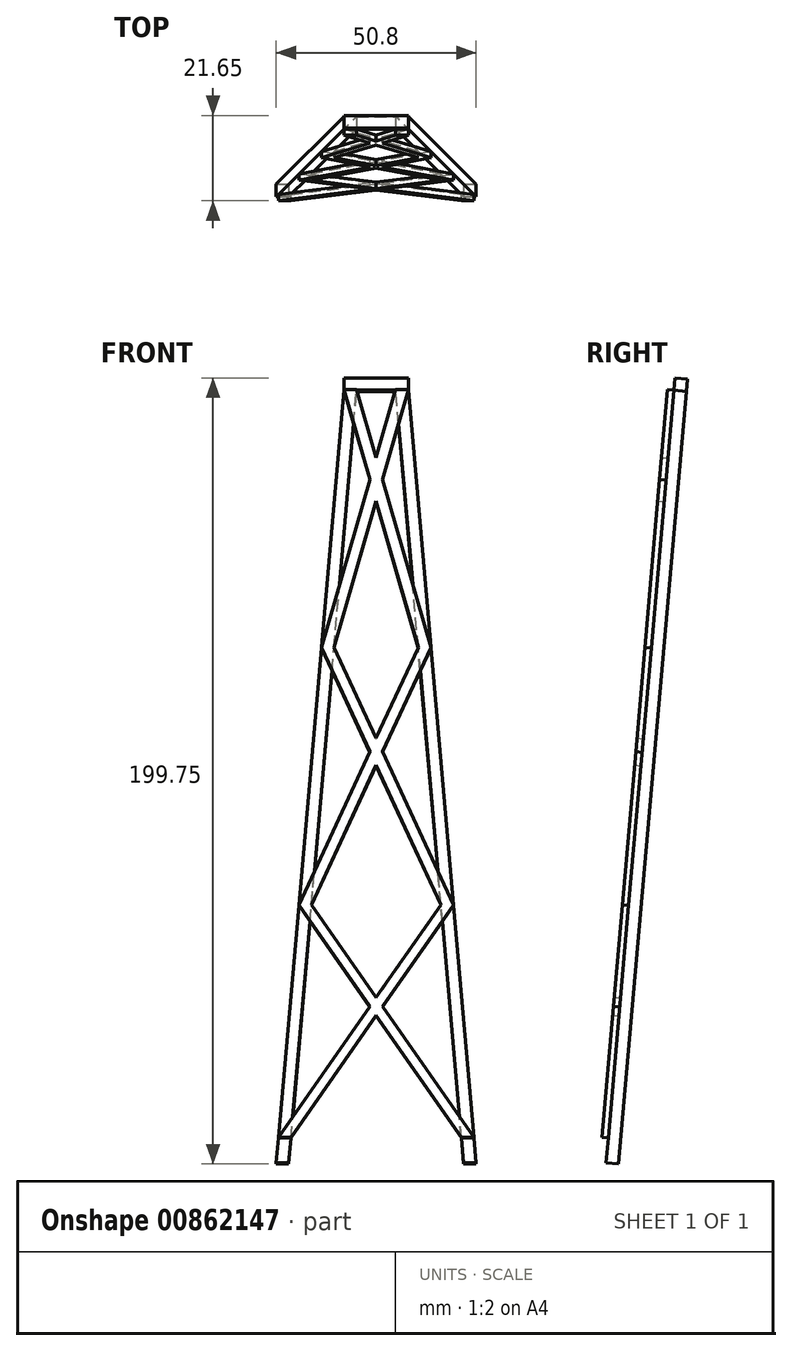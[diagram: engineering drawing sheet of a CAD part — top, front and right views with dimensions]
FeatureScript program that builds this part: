
annotation { "Feature Type Name" : "Feature", "Feature Type Description" : "" }
export const myFeature = defineFeature(function(context is Context, id is Id, definition is map)
    precondition{}
    {
        {
            var Q0;
            Q0=qCreatedBy(makeId("Top.planeOp"),FACE);
            var sketch = newSketch(context, id + "F0", { "sketchPlane" : qUnion([Q0])});
            skLineSegment(sketch, "E0", {"start": v(0, 0) * mm, "end": v(0, 116.82) * mm, "construction": true});
            skLineSegment(sketch, "E1", {"start": v(0, 0) * mm, "end": v(-140.82, 0) * mm, "construction": true});
            skSolve(sketch);
        }
        {
            var Q0;
            Q0=qCreatedBy(makeId("Right.planeOp"),FACE);
            var sketch = newSketch(context, id + "F1", { "sketchPlane" : qUnion([Q0])});
            skLineSegment(sketch, "E2", {"start": v(0, 0) * mm, "end": v(0, 196.85) * mm, "construction": true});
            skSolve(sketch);
        }
        {
            var Q0;
            Q0=qCreatedBy(makeId("Right.planeOp"),FACE);
            var sketch = newSketch(context, id + "F2", { "sketchPlane" : qUnion([Q0])});
            skPoint(sketch, "E3", {"position": v(-25.4, 0) * mm});
            skPoint(sketch, "E4.MirrorP", {"position": v(25.4, 0) * mm});
            skPoint(sketch, "E5", {"position": v(0, 290.32) * mm});
            skLineSegment(sketch, "E6", {"start": v(0, 290.32) * mm, "end": v(-25.4, 0) * mm, "construction": true});
            skLineSegment(sketch, "E7", {"start": v(0, 197.07) * mm, "end": v(-8.16, 197.07) * mm, "construction": true});
            skSolve(sketch);
        }
        {
            var Q0;
            Q0=sQuery(id+"F2.wireOp",EDGE,"E6");
            cPlane(context, id + "F3", {"entities" : qUnion([Q0]), "cplaneType" : CPlaneType.LINE_ANGLE, "offset" : 25.4 * mm, "angle" : 270 * degree, "width" : 152.4 * mm, "height" : 152.4 * mm});
        }
        {
            var Q0;
            Q0=qCreatedBy(id+"F3.planeOp",FACE);
            var sketch = newSketch(context, id + "F4", { "sketchPlane" : qUnion([Q0])});
            skLineSegment(sketch, "E8", {"start": v(-8.16, 197.06) * mm, "end": v(-25.4, 0) * mm});
            skLineSegment(sketch, "E9.0", {"start": v(-22.21, 0) * mm, "end": v(-4.97, 197.06) * mm});
            skLineSegment(sketch, "E10", {"start": v(-25.4, 0) * mm, "end": v(-22.24, 0) * mm});
            skPoint(sketch, "E11.orphan", {"position": v(0, 290.32) * mm});
            skLineSegment(sketch, "E12.MirrorCS", {"start": v(8.16, 197.06) * mm, "end": v(25.4, 0) * mm});
            skLineSegment(sketch, "E13.MirrorCS", {"start": v(22.21, 0) * mm, "end": v(4.97, 197.06) * mm});
            skLineSegment(sketch, "E14", {"start": v(-8.16, 197.06) * mm, "end": v(-4.97, 197.06) * mm});
            skLineSegment(sketch, "E15", {"start": v(-25.4, 0) * mm, "end": v(-22.21, 0) * mm});
            skLineSegment(sketch, "E16", {"start": v(4.97, 197.06) * mm, "end": v(8.16, 197.06) * mm});
            skLineSegment(sketch, "E17", {"start": v(22.21, 0) * mm, "end": v(25.4, 0) * mm});
            skLineSegment(sketch, "E18", {"start": v(-8.16, 197.06) * mm, "end": v(8.16, 197.06) * mm});
            skLineSegment(sketch, "E19", {"start": v(8.16, 200.23) * mm, "end": v(8.16, 197.06) * mm});
            skLineSegment(sketch, "E20", {"start": v(8.16, 200.23) * mm, "end": v(-8.16, 200.23) * mm});
            skLineSegment(sketch, "E21", {"start": v(-8.16, 200.23) * mm, "end": v(-8.16, 197.06) * mm});
            skLineSegment(sketch, "E22", {"start": v(52.04, 197.06) * mm, "end": v(52.04, 0) * mm, "construction": true});
            skLineSegment(sketch, "E23", {"start": v(31.34, 0) * mm, "end": v(31.34, 6.35) * mm, "construction": true});
            skLineSegment(sketch, "E24", {"start": v(31.34, 6.35) * mm, "end": v(-63.34, 6.35) * mm, "construction": true});
            skLineSegment(sketch, "E25", {"start": v(24.84, 6.35) * mm, "end": v(21.66, 6.35) * mm});
            skLineSegment(sketch, "E26", {"start": v(40.88, 197.06) * mm, "end": v(40.88, 131.37) * mm, "construction": true});
            skLineSegment(sketch, "E27", {"start": v(40.88, 131.37) * mm, "end": v(40.88, 65.69) * mm, "construction": true});
            skLineSegment(sketch, "E28", {"start": v(40.88, 65.69) * mm, "end": v(40.88, 0) * mm, "construction": true});
            skLineSegment(sketch, "E29", {"start": v(40.88, 65.69) * mm, "end": v(-70.33, 65.69) * mm, "construction": true});
            skLineSegment(sketch, "E30", {"start": v(40.88, 131.37) * mm, "end": v(-29.1, 131.37) * mm, "construction": true});
            skLineSegment(sketch, "E31", {"start": v(-4.97, 197.06) * mm, "end": v(13.9, 131.37) * mm});
            skLineSegment(sketch, "E32", {"start": v(13.9, 131.37) * mm, "end": v(10.72, 131.37) * mm});
            skLineSegment(sketch, "E33", {"start": v(10.72, 131.37) * mm, "end": v(-8.16, 197.06) * mm});
            skLineSegment(sketch, "E34", {"start": v(-10.72, 131.37) * mm, "end": v(19.65, 65.69) * mm});
            skLineSegment(sketch, "E35", {"start": v(19.65, 65.69) * mm, "end": v(16.47, 65.69) * mm});
            skLineSegment(sketch, "E36", {"start": v(16.47, 65.69) * mm, "end": v(-13.9, 131.37) * mm});
            skLineSegment(sketch, "E37", {"start": v(-13.9, 131.37) * mm, "end": v(-10.72, 131.37) * mm});
            skLineSegment(sketch, "E38", {"start": v(-16.47, 65.69) * mm, "end": v(24.84, 6.35) * mm});
            skLineSegment(sketch, "E39", {"start": v(21.66, 6.35) * mm, "end": v(-19.65, 65.69) * mm});
            skLineSegment(sketch, "E40", {"start": v(-19.65, 65.69) * mm, "end": v(-16.47, 65.69) * mm});
            skLineSegment(sketch, "E41", {"start": v(4.97, 197.06) * mm, "end": v(-13.9, 131.37) * mm});
            skLineSegment(sketch, "E42", {"start": v(-10.72, 131.37) * mm, "end": v(8.16, 197.06) * mm});
            skLineSegment(sketch, "E43", {"start": v(-19.65, 65.69) * mm, "end": v(10.72, 131.37) * mm});
            skLineSegment(sketch, "E44", {"start": v(13.9, 131.37) * mm, "end": v(-16.47, 65.69) * mm});
            skLineSegment(sketch, "E45", {"start": v(16.47, 65.69) * mm, "end": v(-24.84, 6.35) * mm});
            skLineSegment(sketch, "E46", {"start": v(-24.84, 6.35) * mm, "end": v(-21.66, 6.35) * mm});
            skLineSegment(sketch, "E47", {"start": v(-21.66, 6.35) * mm, "end": v(19.65, 65.69) * mm});
            skSolve(sketch);
        }
        {
            var Q0;
            {var subQ0=sQuery(id+"F4.wireOp",EDGE,"E19");Q0=makeQuery(id+"F4.imprint","IMPRINT",FACE,{"disambiguationData":[TD([[makeQuery(id+"F4.imprint","IMPRINT",EDGE,{"derivedFrom":subQ0}),-1.0]])]});}
            extrude(context, id + "F5", {"entities" : qUnion([Q0]), "oppositeDirection" : true, "depth" : 3.17 * mm, "offsetDistance" : 25.4 * mm});
        }
        {
            var Q0;
            {var subQ1=sQuery(id+"F4.wireOp",EDGE,"E9.0");var subQ3=sQuery(id+"F4.wireOp",EDGE,"E33");var subQ4=makeQuery(id+"F4.imprint","INTERSECT",VERTEX,{"derivedFrom":[subQ1,subQ3]});Q0=makeQuery(id+"F4.imprint","IMPRINT",FACE,{"disambiguationData":[TD([[makeQuery(id+"F4.imprint","IMPRINT",EDGE,{"disambiguationData":[TD([[subQ4,-1.0]])],"derivedFrom":subQ1}),1.0]])]});}
            var Q1;
            {var subQ3=sQuery(id+"F4.wireOp",EDGE,"E41");var subQ5=sQuery(id+"F4.wireOp",EDGE,"E9.0");var subQ6=makeQuery(id+"F4.imprint","INTERSECT",VERTEX,{"derivedFrom":[subQ5,subQ3]});Q1=makeQuery(id+"F4.imprint","IMPRINT",FACE,{"disambiguationData":[TD([[makeQuery(id+"F4.imprint","IMPRINT",EDGE,{"disambiguationData":[TD([[subQ6,-1.0]])],"derivedFrom":subQ5}),1.0]])]});}
            var Q2;
            {var subQ1=sQuery(id+"F4.wireOp",EDGE,"E13.MirrorCS");var subQ3=sQuery(id+"F4.wireOp",EDGE,"E42");var subQ4=makeQuery(id+"F4.imprint","INTERSECT",VERTEX,{"derivedFrom":[subQ1,subQ3]});Q2=makeQuery(id+"F4.imprint","IMPRINT",FACE,{"disambiguationData":[TD([[makeQuery(id+"F4.imprint","IMPRINT",EDGE,{"disambiguationData":[TD([[subQ4,-1.0]])],"derivedFrom":subQ1}),-1.0]])]});}
            var Q3;
            {var subQ3=sQuery(id+"F4.wireOp",EDGE,"E31");var subQ5=sQuery(id+"F4.wireOp",EDGE,"E13.MirrorCS");var subQ6=makeQuery(id+"F4.imprint","INTERSECT",VERTEX,{"derivedFrom":[subQ5,subQ3]});Q3=makeQuery(id+"F4.imprint","IMPRINT",FACE,{"disambiguationData":[TD([[makeQuery(id+"F4.imprint","IMPRINT",EDGE,{"disambiguationData":[TD([[subQ6,-1.0]])],"derivedFrom":subQ5}),-1.0]])]});}
            var Q4;
            {var subQ0=sQuery(id+"F4.wireOp",EDGE,"E32");Q4=makeQuery(id+"F4.imprint","IMPRINT",FACE,{"disambiguationData":[TD([[makeQuery(id+"F4.imprint","IMPRINT",EDGE,{"derivedFrom":subQ0}),-1.0]])]});}
            var Q5;
            {var subQ0=sQuery(id+"F4.wireOp",EDGE,"E32");Q5=makeQuery(id+"F4.imprint","IMPRINT",FACE,{"disambiguationData":[TD([[makeQuery(id+"F4.imprint","IMPRINT",EDGE,{"derivedFrom":subQ0}),1.0]])]});}
            var Q6;
            {var subQ0=sQuery(id+"F4.wireOp",EDGE,"E37");Q6=makeQuery(id+"F4.imprint","IMPRINT",FACE,{"disambiguationData":[TD([[makeQuery(id+"F4.imprint","IMPRINT",EDGE,{"derivedFrom":subQ0}),1.0]])]});}
            var Q7;
            {var subQ0=sQuery(id+"F4.wireOp",EDGE,"E37");Q7=makeQuery(id+"F4.imprint","IMPRINT",FACE,{"disambiguationData":[TD([[makeQuery(id+"F4.imprint","IMPRINT",EDGE,{"derivedFrom":subQ0}),-1.0]])]});}
            var Q8;
            {var subQ3=sQuery(id+"F4.wireOp",EDGE,"E43");var subQ5=sQuery(id+"F4.wireOp",EDGE,"E9.0");var subQ6=makeQuery(id+"F4.imprint","INTERSECT",VERTEX,{"derivedFrom":[subQ5,subQ3]});Q8=makeQuery(id+"F4.imprint","IMPRINT",FACE,{"disambiguationData":[TD([[makeQuery(id+"F4.imprint","IMPRINT",EDGE,{"disambiguationData":[TD([[subQ6,-1.0]])],"derivedFrom":subQ5}),1.0]])]});}
            var Q9;
            {var subQ3=sQuery(id+"F4.wireOp",EDGE,"E34");var subQ5=sQuery(id+"F4.wireOp",EDGE,"E13.MirrorCS");var subQ6=makeQuery(id+"F4.imprint","INTERSECT",VERTEX,{"derivedFrom":[subQ5,subQ3]});Q9=makeQuery(id+"F4.imprint","IMPRINT",FACE,{"disambiguationData":[TD([[makeQuery(id+"F4.imprint","IMPRINT",EDGE,{"disambiguationData":[TD([[subQ6,-1.0]])],"derivedFrom":subQ5}),-1.0]])]});}
            var Q10;
            {var subQ0=sQuery(id+"F4.wireOp",EDGE,"E35");Q10=makeQuery(id+"F4.imprint","IMPRINT",FACE,{"disambiguationData":[TD([[makeQuery(id+"F4.imprint","IMPRINT",EDGE,{"derivedFrom":subQ0}),-1.0]])]});}
            var Q11;
            {var subQ0=sQuery(id+"F4.wireOp",EDGE,"E40");Q11=makeQuery(id+"F4.imprint","IMPRINT",FACE,{"disambiguationData":[TD([[makeQuery(id+"F4.imprint","IMPRINT",EDGE,{"derivedFrom":subQ0}),1.0]])]});}
            var Q12;
            {var subQ0=sQuery(id+"F4.wireOp",EDGE,"E40");Q12=makeQuery(id+"F4.imprint","IMPRINT",FACE,{"disambiguationData":[TD([[makeQuery(id+"F4.imprint","IMPRINT",EDGE,{"derivedFrom":subQ0}),-1.0]])]});}
            var Q13;
            {var subQ0=sQuery(id+"F4.wireOp",EDGE,"E35");Q13=makeQuery(id+"F4.imprint","IMPRINT",FACE,{"disambiguationData":[TD([[makeQuery(id+"F4.imprint","IMPRINT",EDGE,{"derivedFrom":subQ0}),1.0]])]});}
            var Q14;
            {var subQ0=sQuery(id+"F4.wireOp",EDGE,"E38");var subQ5=sQuery(id+"F4.wireOp",EDGE,"E13.MirrorCS");var subQ6=makeQuery(id+"F4.imprint","INTERSECT",VERTEX,{"derivedFrom":[subQ5,subQ0]});Q14=makeQuery(id+"F4.imprint","IMPRINT",FACE,{"disambiguationData":[TD([[makeQuery(id+"F4.imprint","IMPRINT",EDGE,{"disambiguationData":[TD([[subQ6,-1.0]])],"derivedFrom":subQ5}),-1.0]])]});}
            var Q15;
            {var subQ3=sQuery(id+"F4.wireOp",EDGE,"E45");var subQ5=sQuery(id+"F4.wireOp",EDGE,"E9.0");var subQ7=makeQuery(id+"F4.imprint","INTERSECT",VERTEX,{"derivedFrom":[subQ5,subQ3]});Q15=makeQuery(id+"F4.imprint","IMPRINT",FACE,{"disambiguationData":[TD([[makeQuery(id+"F4.imprint","IMPRINT",EDGE,{"disambiguationData":[TD([[subQ7,-1.0]])],"derivedFrom":subQ5}),1.0]])]});}
            var Q16;
            {var subQ0=sQuery(id+"F4.wireOp",EDGE,"E46");Q16=makeQuery(id+"F4.imprint","IMPRINT",FACE,{"disambiguationData":[TD([[makeQuery(id+"F4.imprint","IMPRINT",EDGE,{"derivedFrom":subQ0}),1.0]])]});}
            var Q17;
            {var subQ0=sQuery(id+"F4.wireOp",EDGE,"E25");Q17=makeQuery(id+"F4.imprint","IMPRINT",FACE,{"disambiguationData":[TD([[makeQuery(id+"F4.imprint","IMPRINT",EDGE,{"derivedFrom":subQ0}),-1.0]])]});}
            var Q18;
            {var subQ0=sQuery(id+"F4.wireOp",EDGE,"E17");Q18=makeQuery(id+"F4.imprint","IMPRINT",FACE,{"disambiguationData":[TD([[makeQuery(id+"F4.imprint","IMPRINT",EDGE,{"derivedFrom":subQ0}),1.0]])]});}
            var Q19;
            {var subQ3=sQuery(id+"F4.wireOp",EDGE,"E46");Q19=makeQuery(id+"F4.imprint","IMPRINT",FACE,{"disambiguationData":[TD([[makeQuery(id+"F4.imprint","IMPRINT",EDGE,{"derivedFrom":subQ3}),-1.0]])]});}
            extrude(context, id + "F6", {"entities" : qUnion([Q0, Q1, Q2, Q3, Q4, Q5, Q6, Q7, Q8, Q9, Q10, Q11, Q12, Q13, Q14, Q15, Q16, Q17, Q18, Q19]), "oppositeDirection" : true, "depth" : 3.17 * mm, "offsetDistance" : 25.4 * mm});
        }
        {
            var Q0;
            {var subQ1=sQuery(id+"F4.wireOp",EDGE,"E9.0");var subQ3=sQuery(id+"F4.wireOp",EDGE,"E33");var subQ4=makeQuery(id+"F4.imprint","INTERSECT",VERTEX,{"derivedFrom":[subQ1,subQ3]});Q0=makeQuery(id+"F4.imprint","IMPRINT",FACE,{"disambiguationData":[TD([[makeQuery(id+"F4.imprint","IMPRINT",EDGE,{"disambiguationData":[TD([[subQ4,-1.0]])],"derivedFrom":subQ1}),1.0]])]});}
            var Q1;
            {var subQ1=sQuery(id+"F4.wireOp",EDGE,"E9.0");var subQ3=sQuery(id+"F4.wireOp",EDGE,"E33");var subQ4=makeQuery(id+"F4.imprint","INTERSECT",VERTEX,{"derivedFrom":[subQ1,subQ3]});Q1=makeQuery(id+"F4.imprint","IMPRINT",FACE,{"disambiguationData":[TD([[makeQuery(id+"F4.imprint","IMPRINT",EDGE,{"disambiguationData":[TD([[subQ4,1.0]])],"derivedFrom":subQ3}),-1.0]])]});}
            var Q2;
            {var subQ0=sQuery(id+"F4.wireOp",EDGE,"E41");var subQ5=sQuery(id+"F4.wireOp",EDGE,"E31");var subQ6=makeQuery(id+"F4.imprint","INTERSECT",VERTEX,{"derivedFrom":[subQ5,subQ0]});Q2=makeQuery(id+"F4.imprint","IMPRINT",FACE,{"disambiguationData":[TD([[makeQuery(id+"F4.imprint","IMPRINT",EDGE,{"disambiguationData":[TD([[subQ6,-1.0]])],"derivedFrom":subQ5}),1.0]])]});}
            var Q3;
            {var subQ1=sQuery(id+"F4.wireOp",EDGE,"E13.MirrorCS");var subQ3=sQuery(id+"F4.wireOp",EDGE,"E42");var subQ4=makeQuery(id+"F4.imprint","INTERSECT",VERTEX,{"derivedFrom":[subQ1,subQ3]});Q3=makeQuery(id+"F4.imprint","IMPRINT",FACE,{"disambiguationData":[TD([[makeQuery(id+"F4.imprint","IMPRINT",EDGE,{"disambiguationData":[TD([[subQ4,-1.0]])],"derivedFrom":subQ1}),-1.0]])]});}
            var Q4;
            {var subQ0=sQuery(id+"F4.wireOp",EDGE,"E41");var subQ1=sQuery(id+"F4.wireOp",EDGE,"E31");var subQ2=makeQuery(id+"F4.imprint","INTERSECT",VERTEX,{"derivedFrom":[subQ1,subQ0]});Q4=makeQuery(id+"F4.imprint","IMPRINT",FACE,{"disambiguationData":[TD([[makeQuery(id+"F4.imprint","IMPRINT",EDGE,{"disambiguationData":[TD([[subQ2,-1.0]])],"derivedFrom":subQ1}),-1.0]])]});}
            var Q5;
            {var subQ0=sQuery(id+"F4.wireOp",EDGE,"E42");var subQ5=sQuery(id+"F4.wireOp",EDGE,"E33");var subQ7=makeQuery(id+"F4.imprint","INTERSECT",VERTEX,{"derivedFrom":[subQ5,subQ0]});Q5=makeQuery(id+"F4.imprint","IMPRINT",FACE,{"disambiguationData":[TD([[makeQuery(id+"F4.imprint","IMPRINT",EDGE,{"disambiguationData":[TD([[subQ7,-1.0]])],"derivedFrom":subQ5}),1.0]])]});}
            var Q6;
            {var subQ0=sQuery(id+"F4.wireOp",EDGE,"E37");Q6=makeQuery(id+"F4.imprint","IMPRINT",FACE,{"disambiguationData":[TD([[makeQuery(id+"F4.imprint","IMPRINT",EDGE,{"derivedFrom":subQ0}),1.0]])]});}
            var Q7;
            {var subQ1=sQuery(id+"F4.wireOp",EDGE,"E13.MirrorCS");var subQ3=sQuery(id+"F4.wireOp",EDGE,"E31");var subQ4=makeQuery(id+"F4.imprint","INTERSECT",VERTEX,{"derivedFrom":[subQ1,subQ3]});Q7=makeQuery(id+"F4.imprint","IMPRINT",FACE,{"disambiguationData":[TD([[makeQuery(id+"F4.imprint","IMPRINT",EDGE,{"disambiguationData":[TD([[subQ4,1.0]])],"derivedFrom":subQ3}),-1.0]])]});}
            var Q8;
            {var subQ0=sQuery(id+"F4.wireOp",EDGE,"E32");Q8=makeQuery(id+"F4.imprint","IMPRINT",FACE,{"disambiguationData":[TD([[makeQuery(id+"F4.imprint","IMPRINT",EDGE,{"derivedFrom":subQ0}),-1.0]])]});}
            var Q9;
            {var subQ0=sQuery(id+"F4.wireOp",EDGE,"E43");var subQ5=sQuery(id+"F4.wireOp",EDGE,"E34");var subQ6=makeQuery(id+"F4.imprint","INTERSECT",VERTEX,{"derivedFrom":[subQ5,subQ0]});Q9=makeQuery(id+"F4.imprint","IMPRINT",FACE,{"disambiguationData":[TD([[makeQuery(id+"F4.imprint","IMPRINT",EDGE,{"disambiguationData":[TD([[subQ6,-1.0]])],"derivedFrom":subQ5}),1.0]])]});}
            var Q10;
            {var subQ0=sQuery(id+"F4.wireOp",EDGE,"E32");Q10=makeQuery(id+"F4.imprint","IMPRINT",FACE,{"disambiguationData":[TD([[makeQuery(id+"F4.imprint","IMPRINT",EDGE,{"derivedFrom":subQ0}),1.0]])]});}
            var Q11;
            {var subQ1=sQuery(id+"F4.wireOp",EDGE,"E9.0");var subQ3=sQuery(id+"F4.wireOp",EDGE,"E36");var subQ4=makeQuery(id+"F4.imprint","INTERSECT",VERTEX,{"derivedFrom":[subQ1,subQ3]});Q11=makeQuery(id+"F4.imprint","IMPRINT",FACE,{"disambiguationData":[TD([[makeQuery(id+"F4.imprint","IMPRINT",EDGE,{"disambiguationData":[TD([[subQ4,1.0]])],"derivedFrom":subQ3}),-1.0]])]});}
            var Q12;
            {var subQ0=sQuery(id+"F4.wireOp",EDGE,"E37");Q12=makeQuery(id+"F4.imprint","IMPRINT",FACE,{"disambiguationData":[TD([[makeQuery(id+"F4.imprint","IMPRINT",EDGE,{"derivedFrom":subQ0}),-1.0]])]});}
            var Q13;
            {var subQ0=sQuery(id+"F4.wireOp",EDGE,"E43");var subQ1=sQuery(id+"F4.wireOp",EDGE,"E34");var subQ2=makeQuery(id+"F4.imprint","INTERSECT",VERTEX,{"derivedFrom":[subQ1,subQ0]});Q13=makeQuery(id+"F4.imprint","IMPRINT",FACE,{"disambiguationData":[TD([[makeQuery(id+"F4.imprint","IMPRINT",EDGE,{"disambiguationData":[TD([[subQ2,-1.0]])],"derivedFrom":subQ1}),-1.0]])]});}
            var Q14;
            {var subQ0=sQuery(id+"F4.wireOp",EDGE,"E44");var subQ5=sQuery(id+"F4.wireOp",EDGE,"E36");var subQ6=makeQuery(id+"F4.imprint","INTERSECT",VERTEX,{"derivedFrom":[subQ5,subQ0]});Q14=makeQuery(id+"F4.imprint","IMPRINT",FACE,{"disambiguationData":[TD([[makeQuery(id+"F4.imprint","IMPRINT",EDGE,{"disambiguationData":[TD([[subQ6,-1.0]])],"derivedFrom":subQ5}),1.0]])]});}
            var Q15;
            {var subQ1=sQuery(id+"F4.wireOp",EDGE,"E13.MirrorCS");var subQ3=sQuery(id+"F4.wireOp",EDGE,"E34");var subQ4=makeQuery(id+"F4.imprint","INTERSECT",VERTEX,{"derivedFrom":[subQ1,subQ3]});Q15=makeQuery(id+"F4.imprint","IMPRINT",FACE,{"disambiguationData":[TD([[makeQuery(id+"F4.imprint","IMPRINT",EDGE,{"disambiguationData":[TD([[subQ4,1.0]])],"derivedFrom":subQ3}),-1.0]])]});}
            var Q16;
            {var subQ0=sQuery(id+"F4.wireOp",EDGE,"E35");Q16=makeQuery(id+"F4.imprint","IMPRINT",FACE,{"disambiguationData":[TD([[makeQuery(id+"F4.imprint","IMPRINT",EDGE,{"derivedFrom":subQ0}),-1.0]])]});}
            var Q17;
            {var subQ0=sQuery(id+"F4.wireOp",EDGE,"E35");Q17=makeQuery(id+"F4.imprint","IMPRINT",FACE,{"disambiguationData":[TD([[makeQuery(id+"F4.imprint","IMPRINT",EDGE,{"derivedFrom":subQ0}),1.0]])]});}
            var Q18;
            {var subQ0=sQuery(id+"F4.wireOp",EDGE,"E45");var subQ5=sQuery(id+"F4.wireOp",EDGE,"E38");var subQ6=makeQuery(id+"F4.imprint","INTERSECT",VERTEX,{"derivedFrom":[subQ5,subQ0]});Q18=makeQuery(id+"F4.imprint","IMPRINT",FACE,{"disambiguationData":[TD([[makeQuery(id+"F4.imprint","IMPRINT",EDGE,{"disambiguationData":[TD([[subQ6,-1.0]])],"derivedFrom":subQ5}),1.0]])]});}
            var Q19;
            {var subQ0=sQuery(id+"F4.wireOp",EDGE,"E40");Q19=makeQuery(id+"F4.imprint","IMPRINT",FACE,{"disambiguationData":[TD([[makeQuery(id+"F4.imprint","IMPRINT",EDGE,{"derivedFrom":subQ0}),1.0]])]});}
            var Q20;
            {var subQ0=sQuery(id+"F4.wireOp",EDGE,"E40");Q20=makeQuery(id+"F4.imprint","IMPRINT",FACE,{"disambiguationData":[TD([[makeQuery(id+"F4.imprint","IMPRINT",EDGE,{"derivedFrom":subQ0}),-1.0]])]});}
            var Q21;
            {var subQ1=sQuery(id+"F4.wireOp",EDGE,"E9.0");var subQ3=sQuery(id+"F4.wireOp",EDGE,"E39");var subQ4=makeQuery(id+"F4.imprint","INTERSECT",VERTEX,{"derivedFrom":[subQ1,subQ3]});Q21=makeQuery(id+"F4.imprint","IMPRINT",FACE,{"disambiguationData":[TD([[makeQuery(id+"F4.imprint","IMPRINT",EDGE,{"disambiguationData":[TD([[subQ4,1.0]])],"derivedFrom":subQ3}),-1.0]])]});}
            var Q22;
            {var subQ0=sQuery(id+"F4.wireOp",EDGE,"E45");var subQ1=sQuery(id+"F4.wireOp",EDGE,"E38");var subQ2=makeQuery(id+"F4.imprint","INTERSECT",VERTEX,{"derivedFrom":[subQ1,subQ0]});Q22=makeQuery(id+"F4.imprint","IMPRINT",FACE,{"disambiguationData":[TD([[makeQuery(id+"F4.imprint","IMPRINT",EDGE,{"disambiguationData":[TD([[subQ2,-1.0]])],"derivedFrom":subQ1}),-1.0]])]});}
            var Q23;
            {var subQ0=sQuery(id+"F4.wireOp",EDGE,"E47");var subQ5=sQuery(id+"F4.wireOp",EDGE,"E39");var subQ6=makeQuery(id+"F4.imprint","INTERSECT",VERTEX,{"derivedFrom":[subQ5,subQ0]});Q23=makeQuery(id+"F4.imprint","IMPRINT",FACE,{"disambiguationData":[TD([[makeQuery(id+"F4.imprint","IMPRINT",EDGE,{"disambiguationData":[TD([[subQ6,-1.0]])],"derivedFrom":subQ5}),1.0]])]});}
            var Q24;
            {var subQ1=sQuery(id+"F4.wireOp",EDGE,"E13.MirrorCS");var subQ3=sQuery(id+"F4.wireOp",EDGE,"E38");var subQ4=makeQuery(id+"F4.imprint","INTERSECT",VERTEX,{"derivedFrom":[subQ1,subQ3]});Q24=makeQuery(id+"F4.imprint","IMPRINT",FACE,{"disambiguationData":[TD([[makeQuery(id+"F4.imprint","IMPRINT",EDGE,{"disambiguationData":[TD([[subQ4,1.0]])],"derivedFrom":subQ3}),-1.0]])]});}
            var Q25;
            {var subQ0=sQuery(id+"F4.wireOp",EDGE,"E46");Q25=makeQuery(id+"F4.imprint","IMPRINT",FACE,{"disambiguationData":[TD([[makeQuery(id+"F4.imprint","IMPRINT",EDGE,{"derivedFrom":subQ0}),1.0]])]});}
            var Q26;
            {var subQ0=sQuery(id+"F4.wireOp",EDGE,"E25");Q26=makeQuery(id+"F4.imprint","IMPRINT",FACE,{"disambiguationData":[TD([[makeQuery(id+"F4.imprint","IMPRINT",EDGE,{"derivedFrom":subQ0}),-1.0]])]});}
            extrude(context, id + "F7", {"entities" : qUnion([Q0, Q1, Q2, Q3, Q4, Q5, Q6, Q7, Q8, Q9, Q10, Q11, Q12, Q13, Q14, Q15, Q16, Q17, Q18, Q19, Q20, Q21, Q22, Q23, Q24, Q25, Q26]), "operationType" : NewBodyOperationType.ADD, "depth" : 1.59 * mm, "offsetDistance" : 25.4 * mm});
        }
    });
